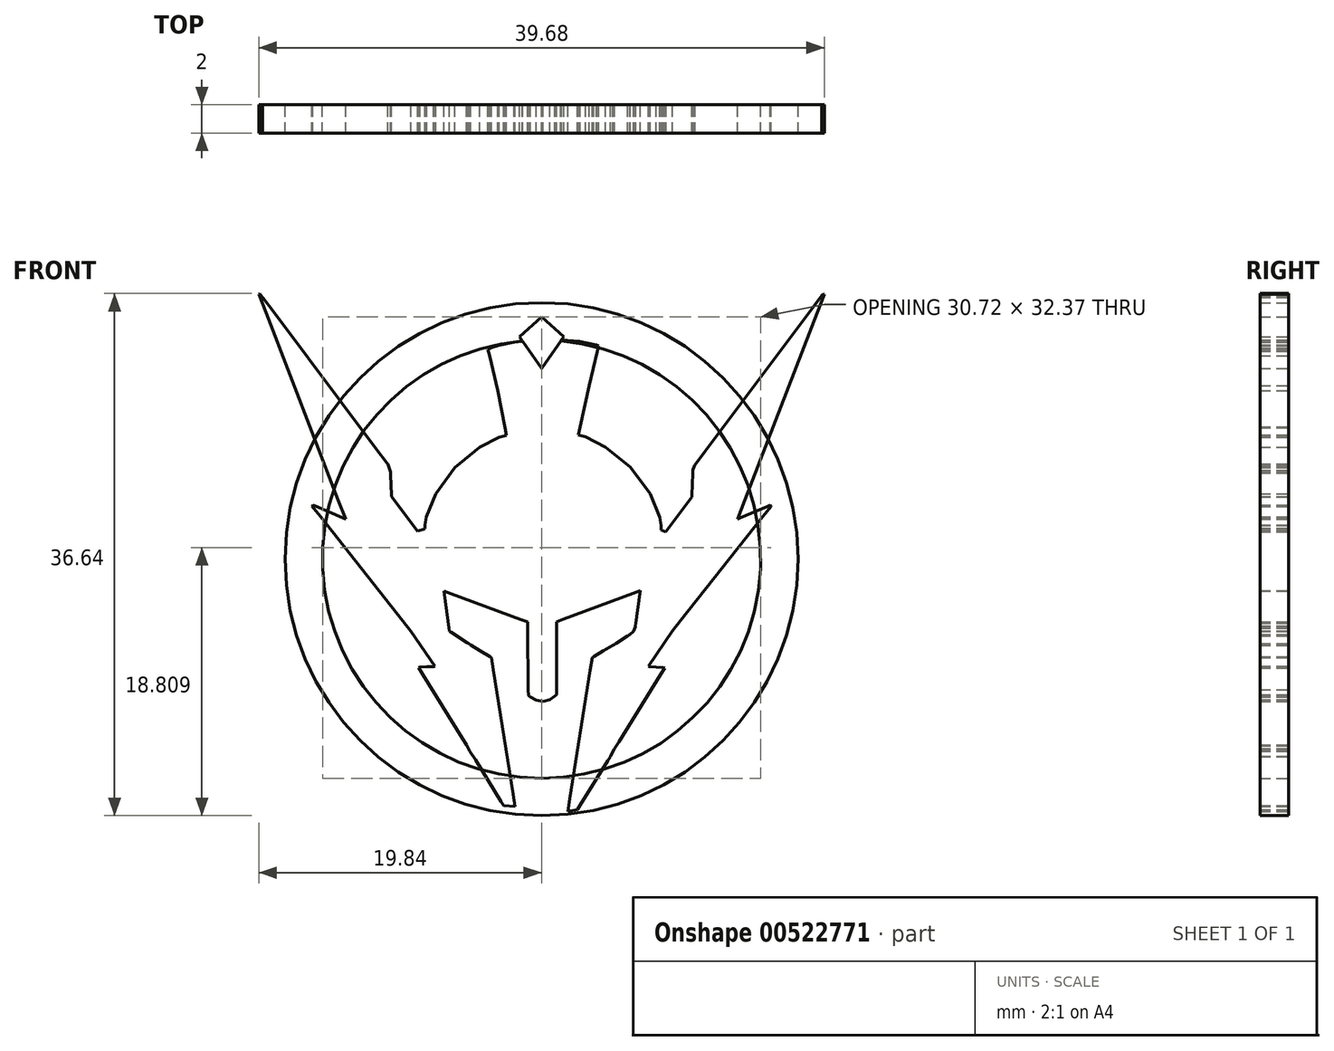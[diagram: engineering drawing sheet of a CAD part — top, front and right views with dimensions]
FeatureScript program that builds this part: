
annotation { "Feature Type Name" : "Feature", "Feature Type Description" : "" }
export const myFeature = defineFeature(function(context is Context, id is Id, definition is map)
    precondition{}
    {
        {
            var Q0;
            Q0=qCreatedBy(makeId("Front.planeOp"),FACE);
            var sketch = newSketch(context, id + "F0", { "sketchPlane" : qUnion([Q0])});
            skLineSegment(sketch, "E0", {"start": v(-19.78, 18.64) * mm, "end": v(-19.78, 18.64) * mm});
            skLineSegment(sketch, "E1", {"start": v(-19.78, 18.64) * mm, "end": v(-19.84, 18.6) * mm});
            skLineSegment(sketch, "E2", {"start": v(-19.84, 18.6) * mm, "end": v(-19.84, 18.6) * mm});
            skLineSegment(sketch, "E3", {"start": v(-19.84, 18.6) * mm, "end": v(-19.34, 17.3) * mm});
            skLineSegment(sketch, "E4", {"start": v(-19.34, 17.3) * mm, "end": v(-14.27, 4.15) * mm});
            skLineSegment(sketch, "E5", {"start": v(-14.27, 4.15) * mm, "end": v(-13.75, 2.82) * mm});
            skLineSegment(sketch, "E6", {"start": v(-13.75, 2.82) * mm, "end": v(-13.96, 2.9) * mm});
            skLineSegment(sketch, "E7", {"start": v(-13.96, 2.9) * mm, "end": v(-15.87, 3.72) * mm});
            skLineSegment(sketch, "E8", {"start": v(-15.87, 3.72) * mm, "end": v(-16.05, 3.8) * mm});
            skLineSegment(sketch, "E9", {"start": v(-16.05, 3.8) * mm, "end": v(-16.05, 3.79) * mm});
            skLineSegment(sketch, "E10", {"start": v(-16.05, 3.79) * mm, "end": v(-16.1, 3.72) * mm});
            skLineSegment(sketch, "E11", {"start": v(-16.1, 3.72) * mm, "end": v(-16.1, 3.72) * mm});
            skLineSegment(sketch, "E12", {"start": v(-16.1, 3.72) * mm, "end": v(-15.53, 2.99) * mm});
            skLineSegment(sketch, "E13", {"start": v(-15.53, 2.99) * mm, "end": v(-9.74, -4.32) * mm});
            skLineSegment(sketch, "E14", {"start": v(-9.74, -4.32) * mm, "end": v(-9.17, -5.05) * mm});
            skLineSegment(sketch, "E15", {"start": v(-9.17, -5.05) * mm, "end": v(-7.5, -7.52) * mm});
            skLineSegment(sketch, "E16", {"start": v(-7.5, -7.52) * mm, "end": v(-7.58, -7.54) * mm});
            skLineSegment(sketch, "E17", {"start": v(-7.58, -7.54) * mm, "end": v(-8.05, -7.55) * mm});
            skLineSegment(sketch, "E18", {"start": v(-8.05, -7.55) * mm, "end": v(-8.54, -7.58) * mm});
            skLineSegment(sketch, "E19", {"start": v(-8.54, -7.58) * mm, "end": v(-8.64, -7.61) * mm});
            skLineSegment(sketch, "E20", {"start": v(-8.64, -7.61) * mm, "end": v(-8.36, -8.07) * mm});
            skLineSegment(sketch, "E21", {"start": v(-8.36, -8.07) * mm, "end": v(-5.54, -12.6) * mm});
            skLineSegment(sketch, "E22", {"start": v(-5.54, -12.6) * mm, "end": v(-5.26, -13.05) * mm});
            skLineSegment(sketch, "E23", {"start": v(-5.26, -13.05) * mm, "end": v(-5.24, -13.1) * mm});
            skLineSegment(sketch, "E24", {"start": v(-5.24, -13.1) * mm, "end": v(-5.04, -13.47) * mm});
            skLineSegment(sketch, "E25", {"start": v(-5.04, -13.47) * mm, "end": v(-4.84, -13.78) * mm});
            skLineSegment(sketch, "E26", {"start": v(-4.84, -13.78) * mm, "end": v(-4.82, -13.8) * mm});
            skLineSegment(sketch, "E27", {"start": v(-4.82, -13.8) * mm, "end": v(-4.64, -14.1) * mm});
            skLineSegment(sketch, "E28", {"start": v(-4.64, -14.1) * mm, "end": v(-2.84, -17) * mm});
            skLineSegment(sketch, "E29", {"start": v(-2.84, -17) * mm, "end": v(-2.66, -17.3) * mm});
            skLineSegment(sketch, "E30", {"start": v(-2.66, -17.3) * mm, "end": v(-1.86, -17.37) * mm});
            skLineSegment(sketch, "E31", {"start": v(-1.86, -17.37) * mm, "end": v(-2, -16.5) * mm});
            skLineSegment(sketch, "E32", {"start": v(-2, -16.5) * mm, "end": v(-3.38, -7.77) * mm});
            skLineSegment(sketch, "E33", {"start": v(-3.38, -7.77) * mm, "end": v(-3.51, -6.9) * mm});
            skLineSegment(sketch, "E34", {"start": v(-3.51, -6.9) * mm, "end": v(-3.63, -6.83) * mm});
            skLineSegment(sketch, "E35", {"start": v(-3.63, -6.83) * mm, "end": v(-4.3, -6.43) * mm});
            skLineSegment(sketch, "E36", {"start": v(-4.3, -6.43) * mm, "end": v(-4.99, -6) * mm});
            skLineSegment(sketch, "E37", {"start": v(-4.99, -6) * mm, "end": v(-5.12, -5.93) * mm});
            skLineSegment(sketch, "E38", {"start": v(-5.12, -5.93) * mm, "end": v(-5.23, -5.85) * mm});
            skLineSegment(sketch, "E39", {"start": v(-5.23, -5.85) * mm, "end": v(-6.36, -5.13) * mm});
            skLineSegment(sketch, "E40", {"start": v(-6.36, -5.13) * mm, "end": v(-6.47, -5.05) * mm});
            skLineSegment(sketch, "E41", {"start": v(-6.47, -5.05) * mm, "end": v(-6.5, -4.82) * mm});
            skLineSegment(sketch, "E42", {"start": v(-6.5, -4.82) * mm, "end": v(-6.8, -2.49) * mm});
            skLineSegment(sketch, "E43", {"start": v(-6.8, -2.49) * mm, "end": v(-6.84, -2.24) * mm});
            skLineSegment(sketch, "E44", {"start": v(-6.84, -2.24) * mm, "end": v(-6.34, -2.43) * mm});
            skLineSegment(sketch, "E45", {"start": v(-6.34, -2.43) * mm, "end": v(-1.46, -4.23) * mm});
            skLineSegment(sketch, "E46", {"start": v(-1.46, -4.23) * mm, "end": v(-0.98, -4.4) * mm});
            skLineSegment(sketch, "E47", {"start": v(-0.98, -4.4) * mm, "end": v(-0.97, -4.85) * mm});
            skLineSegment(sketch, "E48", {"start": v(-0.97, -4.85) * mm, "end": v(-0.95, -9.16) * mm});
            skLineSegment(sketch, "E49", {"start": v(-0.95, -9.16) * mm, "end": v(-0.93, -9.58) * mm});
            skLineSegment(sketch, "E50", {"start": v(-0.93, -9.58) * mm, "end": v(-0.8, -9.67) * mm});
            skLineSegment(sketch, "E51", {"start": v(-0.8, -9.67) * mm, "end": v(-0.36, -9.89) * mm});
            skLineSegment(sketch, "E52", {"start": v(-0.36, -9.89) * mm, "end": v(0.11, -9.98) * mm});
            skLineSegment(sketch, "E53", {"start": v(0.11, -9.98) * mm, "end": v(0.57, -9.86) * mm});
            skLineSegment(sketch, "E54", {"start": v(0.57, -9.86) * mm, "end": v(0.94, -9.6) * mm});
            skLineSegment(sketch, "E55", {"start": v(0.94, -9.6) * mm, "end": v(1.05, -9.51) * mm});
            skLineSegment(sketch, "E56", {"start": v(1.05, -9.51) * mm, "end": v(1.05, -4.4) * mm});
            skLineSegment(sketch, "E57", {"start": v(1.05, -4.4) * mm, "end": v(1.54, -4.22) * mm});
            skLineSegment(sketch, "E58", {"start": v(1.54, -4.22) * mm, "end": v(6.42, -2.4) * mm});
            skLineSegment(sketch, "E59", {"start": v(6.42, -2.4) * mm, "end": v(6.92, -2.2) * mm});
            skLineSegment(sketch, "E60", {"start": v(6.92, -2.2) * mm, "end": v(6.89, -2.43) * mm});
            skLineSegment(sketch, "E61", {"start": v(6.89, -2.43) * mm, "end": v(6.6, -4.48) * mm});
            skLineSegment(sketch, "E62", {"start": v(6.6, -4.48) * mm, "end": v(6.58, -4.68) * mm});
            skLineSegment(sketch, "E63", {"start": v(6.58, -4.68) * mm, "end": v(6.57, -4.75) * mm});
            skLineSegment(sketch, "E64", {"start": v(6.57, -4.75) * mm, "end": v(6.45, -5.06) * mm});
            skLineSegment(sketch, "E65", {"start": v(6.45, -5.06) * mm, "end": v(6.21, -5.29) * mm});
            skLineSegment(sketch, "E66", {"start": v(6.21, -5.29) * mm, "end": v(6.14, -5.33) * mm});
            skLineSegment(sketch, "E67", {"start": v(6.14, -5.33) * mm, "end": v(6.06, -5.37) * mm});
            skLineSegment(sketch, "E68", {"start": v(6.06, -5.37) * mm, "end": v(5.2, -5.92) * mm});
            skLineSegment(sketch, "E69", {"start": v(5.2, -5.92) * mm, "end": v(5.11, -5.98) * mm});
            skLineSegment(sketch, "E70", {"start": v(5.11, -5.98) * mm, "end": v(5, -6.05) * mm});
            skLineSegment(sketch, "E71", {"start": v(5, -6.05) * mm, "end": v(4.33, -6.44) * mm});
            skLineSegment(sketch, "E72", {"start": v(4.33, -6.44) * mm, "end": v(3.66, -6.83) * mm});
            skLineSegment(sketch, "E73", {"start": v(3.66, -6.83) * mm, "end": v(3.55, -6.9) * mm});
            skLineSegment(sketch, "E74", {"start": v(3.55, -6.9) * mm, "end": v(3.41, -7.8) * mm});
            skLineSegment(sketch, "E75", {"start": v(3.41, -7.8) * mm, "end": v(1.99, -16.82) * mm});
            skLineSegment(sketch, "E76", {"start": v(1.99, -16.82) * mm, "end": v(1.85, -17.72) * mm});
            skLineSegment(sketch, "E77", {"start": v(1.85, -17.72) * mm, "end": v(2.52, -17.57) * mm});
            skLineSegment(sketch, "E78", {"start": v(2.52, -17.57) * mm, "end": v(2.7, -17.26) * mm});
            skLineSegment(sketch, "E79", {"start": v(2.7, -17.26) * mm, "end": v(4.64, -14.16) * mm});
            skLineSegment(sketch, "E80", {"start": v(4.64, -14.16) * mm, "end": v(4.83, -13.85) * mm});
            skLineSegment(sketch, "E81", {"start": v(4.83, -13.85) * mm, "end": v(4.85, -13.83) * mm});
            skLineSegment(sketch, "E82", {"start": v(4.85, -13.83) * mm, "end": v(5.1, -13.35) * mm});
            skLineSegment(sketch, "E83", {"start": v(5.1, -13.35) * mm, "end": v(5.12, -13.3) * mm});
            skLineSegment(sketch, "E84", {"start": v(5.12, -13.3) * mm, "end": v(5.42, -12.82) * mm});
            skLineSegment(sketch, "E85", {"start": v(5.42, -12.82) * mm, "end": v(8.35, -8.1) * mm});
            skLineSegment(sketch, "E86", {"start": v(8.35, -8.1) * mm, "end": v(8.64, -7.62) * mm});
            skLineSegment(sketch, "E87", {"start": v(8.64, -7.62) * mm, "end": v(8.53, -7.6) * mm});
            skLineSegment(sketch, "E88", {"start": v(8.53, -7.6) * mm, "end": v(8.03, -7.58) * mm});
            skLineSegment(sketch, "E89", {"start": v(8.03, -7.58) * mm, "end": v(7.58, -7.55) * mm});
            skLineSegment(sketch, "E90", {"start": v(7.58, -7.55) * mm, "end": v(7.5, -7.52) * mm});
            skLineSegment(sketch, "E91", {"start": v(7.5, -7.52) * mm, "end": v(9.19, -5.03) * mm});
            skLineSegment(sketch, "E92", {"start": v(9.19, -5.03) * mm, "end": v(9.76, -4.3) * mm});
            skLineSegment(sketch, "E93", {"start": v(9.76, -4.3) * mm, "end": v(15.53, 2.98) * mm});
            skLineSegment(sketch, "E94", {"start": v(15.53, 2.98) * mm, "end": v(16.1, 3.71) * mm});
            skLineSegment(sketch, "E95", {"start": v(16.1, 3.71) * mm, "end": v(16.1, 3.72) * mm});
            skLineSegment(sketch, "E96", {"start": v(16.1, 3.72) * mm, "end": v(16.05, 3.78) * mm});
            skLineSegment(sketch, "E97", {"start": v(16.05, 3.78) * mm, "end": v(16.05, 3.79) * mm});
            skLineSegment(sketch, "E98", {"start": v(16.05, 3.79) * mm, "end": v(15.86, 3.7) * mm});
            skLineSegment(sketch, "E99", {"start": v(15.86, 3.7) * mm, "end": v(13.96, 2.9) * mm});
            skLineSegment(sketch, "E100", {"start": v(13.96, 2.9) * mm, "end": v(13.76, 2.82) * mm});
            skLineSegment(sketch, "E101", {"start": v(13.76, 2.82) * mm, "end": v(14.27, 4.15) * mm});
            skLineSegment(sketch, "E102", {"start": v(14.27, 4.15) * mm, "end": v(19.34, 17.28) * mm});
            skLineSegment(sketch, "E103", {"start": v(19.34, 17.28) * mm, "end": v(19.84, 18.59) * mm});
            skLineSegment(sketch, "E104", {"start": v(19.84, 18.59) * mm, "end": v(19.82, 18.59) * mm});
            skLineSegment(sketch, "E105", {"start": v(19.82, 18.59) * mm, "end": v(19.67, 18.5) * mm});
            skLineSegment(sketch, "E106", {"start": v(19.67, 18.5) * mm, "end": v(19.66, 18.49) * mm});
            skLineSegment(sketch, "E107", {"start": v(19.66, 18.49) * mm, "end": v(18.92, 17.5) * mm});
            skLineSegment(sketch, "E108", {"start": v(18.92, 17.5) * mm, "end": v(11.5, 7.6) * mm});
            skLineSegment(sketch, "E109", {"start": v(11.5, 7.6) * mm, "end": v(10.76, 6.62) * mm});
            skLineSegment(sketch, "E110", {"start": v(10.76, 6.62) * mm, "end": v(10.73, 6.59) * mm});
            skLineSegment(sketch, "E111", {"start": v(10.73, 6.59) * mm, "end": v(10.61, 6.22) * mm});
            skLineSegment(sketch, "E112", {"start": v(10.61, 6.22) * mm, "end": v(10.61, 6.18) * mm});
            skLineSegment(sketch, "E113", {"start": v(10.61, 6.18) * mm, "end": v(10.6, 6.03) * mm});
            skLineSegment(sketch, "E114", {"start": v(10.6, 6.03) * mm, "end": v(10.54, 4.5) * mm});
            skLineSegment(sketch, "E115", {"start": v(10.54, 4.5) * mm, "end": v(10.53, 4.35) * mm});
            skLineSegment(sketch, "E116", {"start": v(10.53, 4.35) * mm, "end": v(8.72, 1.94) * mm});
            skLineSegment(sketch, "E117", {"start": v(8.72, 1.94) * mm, "end": v(8.72, 1.93) * mm});
            skLineSegment(sketch, "E118", {"start": v(8.72, 1.93) * mm, "end": v(8.38, 2.05) * mm});
            skLineSegment(sketch, "E119", {"start": v(8.38, 2.05) * mm, "end": v(8.38, 2.08) * mm});
            skLineSegment(sketch, "E120", {"start": v(8.38, 2.08) * mm, "end": v(8.37, 2.34) * mm});
            skLineSegment(sketch, "E121", {"start": v(8.37, 2.34) * mm, "end": v(8.37, 2.38) * mm});
            skLineSegment(sketch, "E122", {"start": v(8.37, 2.38) * mm, "end": v(8.29, 2.94) * mm});
            skLineSegment(sketch, "E123", {"start": v(8.29, 2.94) * mm, "end": v(7.62, 4.58) * mm});
            skLineSegment(sketch, "E124", {"start": v(7.62, 4.58) * mm, "end": v(6.23, 6.45) * mm});
            skLineSegment(sketch, "E125", {"start": v(6.23, 6.45) * mm, "end": v(4.47, 7.87) * mm});
            skLineSegment(sketch, "E126", {"start": v(4.47, 7.87) * mm, "end": v(3.08, 8.57) * mm});
            skLineSegment(sketch, "E127", {"start": v(3.08, 8.57) * mm, "end": v(2.6, 8.7) * mm});
            skLineSegment(sketch, "E128", {"start": v(2.6, 8.7) * mm, "end": v(2.71, 9.3) * mm});
            skLineSegment(sketch, "E129", {"start": v(2.71, 9.3) * mm, "end": v(3.35, 12.17) * mm});
            skLineSegment(sketch, "E130", {"start": v(3.35, 12.17) * mm, "end": v(3.92, 14.6) * mm});
            skLineSegment(sketch, "E131", {"start": v(3.92, 14.6) * mm, "end": v(4.02, 14.96) * mm});
            skLineSegment(sketch, "E132", {"start": v(4.02, 14.96) * mm, "end": v(3.86, 15.03) * mm});
            skLineSegment(sketch, "E133", {"start": v(3.86, 15.03) * mm, "end": v(2.64, 15.29) * mm});
            skLineSegment(sketch, "E134", {"start": v(2.64, 15.29) * mm, "end": v(1.04, 15.4) * mm});
            skLineSegment(sketch, "E135", {"start": v(1.04, 15.4) * mm, "end": v(0.7, 15.4) * mm});
            skLineSegment(sketch, "E136", {"start": v(0.7, 15.4) * mm, "end": v(0.36, 15.4) * mm});
            skLineSegment(sketch, "E137", {"start": v(0.36, 15.4) * mm, "end": v(-0.64, 15.35) * mm});
            skLineSegment(sketch, "E138", {"start": v(-0.64, 15.35) * mm, "end": v(-1.92, 15.23) * mm});
            skLineSegment(sketch, "E139", {"start": v(-1.92, 15.23) * mm, "end": v(-3, 15.02) * mm});
            skLineSegment(sketch, "E140", {"start": v(-3, 15.02) * mm, "end": v(-3.6, 14.82) * mm});
            skLineSegment(sketch, "E141", {"start": v(-3.6, 14.82) * mm, "end": v(-3.77, 14.72) * mm});
            skLineSegment(sketch, "E142", {"start": v(-3.77, 14.72) * mm, "end": v(-3.64, 14.28) * mm});
            skLineSegment(sketch, "E143", {"start": v(-3.64, 14.28) * mm, "end": v(-3.07, 11.84) * mm});
            skLineSegment(sketch, "E144", {"start": v(-3.07, 11.84) * mm, "end": v(-2.57, 9.23) * mm});
            skLineSegment(sketch, "E145", {"start": v(-2.57, 9.23) * mm, "end": v(-2.48, 8.7) * mm});
            skLineSegment(sketch, "E146", {"start": v(-2.48, 8.7) * mm, "end": v(-2.97, 8.56) * mm});
            skLineSegment(sketch, "E147", {"start": v(-2.97, 8.56) * mm, "end": v(-4.34, 7.84) * mm});
            skLineSegment(sketch, "E148", {"start": v(-4.34, 7.84) * mm, "end": v(-6.07, 6.43) * mm});
            skLineSegment(sketch, "E149", {"start": v(-6.07, 6.43) * mm, "end": v(-7.43, 4.57) * mm});
            skLineSegment(sketch, "E150", {"start": v(-7.43, 4.57) * mm, "end": v(-8.09, 2.96) * mm});
            skLineSegment(sketch, "E151", {"start": v(-8.09, 2.96) * mm, "end": v(-8.17, 2.4) * mm});
            skLineSegment(sketch, "E152", {"start": v(-8.17, 2.4) * mm, "end": v(-8.18, 2.37) * mm});
            skLineSegment(sketch, "E153", {"start": v(-8.18, 2.37) * mm, "end": v(-8.18, 2.16) * mm});
            skLineSegment(sketch, "E154", {"start": v(-8.18, 2.16) * mm, "end": v(-8.18, 2.14) * mm});
            skLineSegment(sketch, "E155", {"start": v(-8.18, 2.14) * mm, "end": v(-8.24, 2.12) * mm});
            skLineSegment(sketch, "E156", {"start": v(-8.24, 2.12) * mm, "end": v(-8.66, 1.97) * mm});
            skLineSegment(sketch, "E157", {"start": v(-8.66, 1.97) * mm, "end": v(-8.7, 1.96) * mm});
            skLineSegment(sketch, "E158", {"start": v(-8.7, 1.96) * mm, "end": v(-10.53, 4.38) * mm});
            skLineSegment(sketch, "E159", {"start": v(-10.53, 4.38) * mm, "end": v(-10.53, 4.52) * mm});
            skLineSegment(sketch, "E160", {"start": v(-10.53, 4.52) * mm, "end": v(-10.58, 5.9) * mm});
            skLineSegment(sketch, "E161", {"start": v(-10.58, 5.9) * mm, "end": v(-10.58, 6.04) * mm});
            skLineSegment(sketch, "E162", {"start": v(-10.58, 6.04) * mm, "end": v(-10.59, 6.1) * mm});
            skLineSegment(sketch, "E163", {"start": v(-10.59, 6.1) * mm, "end": v(-10.8, 6.68) * mm});
            skLineSegment(sketch, "E164", {"start": v(-10.8, 6.68) * mm, "end": v(-10.84, 6.74) * mm});
            skLineSegment(sketch, "E165", {"start": v(-10.84, 6.74) * mm, "end": v(-11.57, 7.7) * mm});
            skLineSegment(sketch, "E166", {"start": v(-11.57, 7.7) * mm, "end": v(-18.82, 17.37) * mm});
            skLineSegment(sketch, "E167", {"start": v(-18.82, 17.37) * mm, "end": v(-19.55, 18.34) * mm});
            skLineSegment(sketch, "E168", {"start": v(-19.55, 18.34) * mm, "end": v(-19.57, 18.37) * mm});
            skLineSegment(sketch, "E169", {"start": v(-19.57, 18.37) * mm, "end": v(-19.76, 18.61) * mm});
            skLineSegment(sketch, "E170", {"start": v(-19.76, 18.61) * mm, "end": v(-19.78, 18.64) * mm});
            skLineSegment(sketch, "E171", {"start": v(0, 13.37) * mm, "end": v(1.56, 15.6) * mm});
            skLineSegment(sketch, "E172", {"start": v(1.56, 15.6) * mm, "end": v(0, 17) * mm});
            skLineSegment(sketch, "E173", {"start": v(0, 17) * mm, "end": v(-1.53, 15.6) * mm});
            skLineSegment(sketch, "E174", {"start": v(-1.53, 15.6) * mm, "end": v(0, 13.37) * mm});
            skSolve(sketch);
        }
        {
            var Q0;
            Q0=qCreatedBy(makeId("Front.planeOp"),FACE);
            var sketch = newSketch(context, id + "F1", { "sketchPlane" : qUnion([Q0])});
            skCircle(sketch, "E175", {"center": v(0, 0) * mm, "radius": 15.37 * mm});
            skCircle(sketch, "E176", {"center": v(0, 0) * mm, "radius": 18 * mm});
            skSolve(sketch);
        }
        {
            var Q0;
            Q0=makeQuery(id+"F0.imprint","IMPRINT",FACE,{"disambiguationData":[TD([[makeQuery(id+"F0.imprint","IMPRINT",EDGE,{"derivedFrom":sQuery(id+"F0.wireOp",EDGE,"E0")}),1.0]])]});
            var Q1;
            Q1 = qSketchRegion(id + "F1", true);
            extrude(context, id + "F2", {"entities" : qUnion([Q0, Q1]), "depth" : 2 * mm, "offsetDistance" : 25 * mm});
        }
        {
            var Q0;
            {var subQ1=sQuery(id+"F0.wireOp",EDGE,"E135");Q0=makeQuery(id+"F0.imprint","IMPRINT",FACE,{"disambiguationData":[TD([[makeQuery(id+"F0.imprint","IMPRINT",EDGE,{"derivedFrom":subQ1}),1.0]])]});}
            var Q1;
            {var subQ1=sQuery(id+"F0.wireOp",EDGE,"E135");Q1=makeQuery(id+"F0.imprint","IMPRINT",FACE,{"disambiguationData":[TD([[makeQuery(id+"F0.imprint","IMPRINT",EDGE,{"derivedFrom":subQ1}),-1.0]])]});}
            extrude(context, id + "F3", {"entities" : qUnion([Q0, Q1]), "depth" : 2 * mm, "offsetDistance" : 25 * mm});
        }
        {
            var Q0;
            Q0=makeQuery(id+"F3.opExtrude","SWEPT_BODY",BODY,{"disambiguationData":[OSD([sQuery(id+"F0.wireOp",EDGE,"E171"),sQuery(id+"F0.wireOp",EDGE,"E172"),sQuery(id+"F0.wireOp",EDGE,"E173"),sQuery(id+"F0.wireOp",EDGE,"E174")])]});
            var Q1;
            Q1=makeQuery(id+"F2.opExtrude","SWEPT_BODY",BODY,{"disambiguationData":[OSD([sQuery(id+"F1.wireOp",EDGE,"E175"),sQuery(id+"F1.wireOp",EDGE,"E176")])]});
            booleanBodies(context, id + "F4", {"operationType" : BooleanOperationType.SUBTRACTION, "tools" : qUnion([Q0]), "targets" : qUnion([Q1])});
        }
    });
